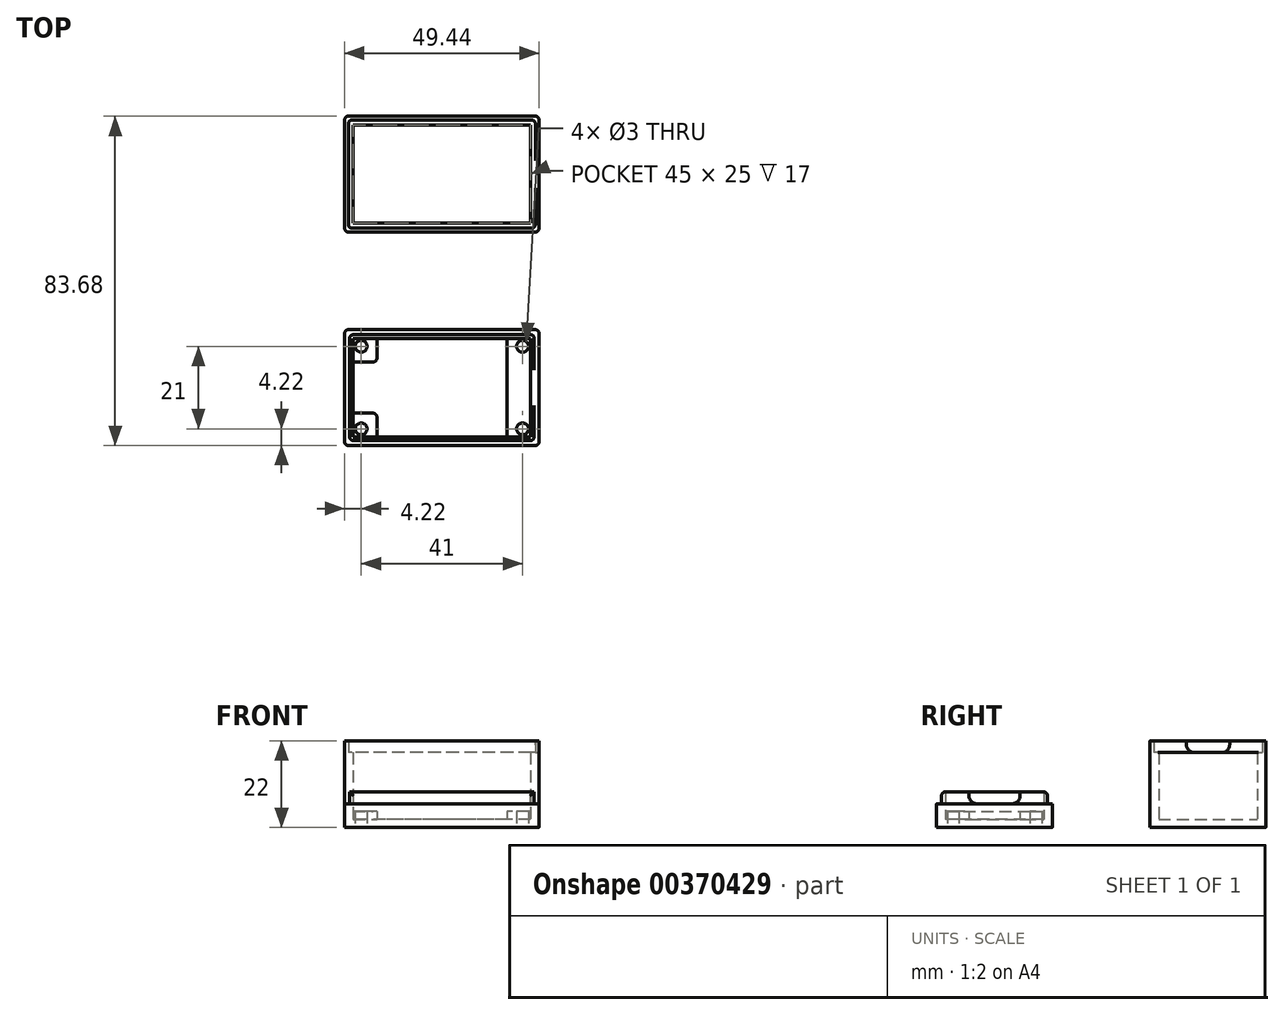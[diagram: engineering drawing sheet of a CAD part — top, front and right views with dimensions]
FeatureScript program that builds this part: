
annotation { "Feature Type Name" : "Feature", "Feature Type Description" : "" }
export const myFeature = defineFeature(function(context is Context, id is Id, definition is map)
    precondition{}
    {
        {
            var Q0;
            Q0=qCreatedBy(makeId("Top.planeOp"),FACE);
            var sketch = newSketch(context, id + "F0", { "sketchPlane" : qUnion([Q0])});
            skLineSegment(sketch, "E0.bottom", {"start": v(22.5, -12.5) * mm, "end": v(-22.5, -12.5) * mm});
            skLineSegment(sketch, "E0.top", {"start": v(22.5, 12.5) * mm, "end": v(-22.5, 12.5) * mm});
            skLineSegment(sketch, "E0.left", {"start": v(22.5, -12.5) * mm, "end": v(22.5, 12.5) * mm});
            skLineSegment(sketch, "E0.right", {"start": v(-22.5, -12.5) * mm, "end": v(-22.5, 12.5) * mm});
            skPoint(sketch, "E0.middle", {"position": v(0, 0) * mm});
            skPoint(sketch, "E1", {"position": v(20.5, 10.5) * mm});
            skPoint(sketch, "E2", {"position": v(-20.5, -10.5) * mm});
            skLineSegment(sketch, "E3", {"start": v(16.5, 12.5) * mm, "end": v(16.5, -12.5) * mm});
            skLineSegment(sketch, "E4", {"start": v(-22.5, 6.5) * mm, "end": v(-16.5, 6.5) * mm});
            skLineSegment(sketch, "E5", {"start": v(-16.5, 6.5) * mm, "end": v(-16.5, 12.5) * mm});
            skLineSegment(sketch, "E6", {"start": v(-22.5, -6.5) * mm, "end": v(-16.5, -6.5) * mm});
            skLineSegment(sketch, "E7", {"start": v(-16.5, -6.5) * mm, "end": v(-16.5, -12.5) * mm});
            skLineSegment(sketch, "E8.0", {"start": v(24.72, 14.72) * mm, "end": v(-24.72, 14.72) * mm});
            skLineSegment(sketch, "E8.1", {"start": v(24.72, -14.72) * mm, "end": v(24.72, 14.72) * mm});
            skLineSegment(sketch, "E8.2", {"start": v(24.72, -14.72) * mm, "end": v(-24.72, -14.72) * mm});
            skLineSegment(sketch, "E8.3", {"start": v(-24.72, -14.72) * mm, "end": v(-24.72, 14.72) * mm});
            skPoint(sketch, "E9", {"position": v(-20.5, 10.5) * mm});
            skPoint(sketch, "E10", {"position": v(20.5, -10.5) * mm});
            skLineSegment(sketch, "E11.bottom", {"start": v(22.5, 41.74) * mm, "end": v(-22.5, 41.74) * mm});
            skLineSegment(sketch, "E11.top", {"start": v(22.5, 66.74) * mm, "end": v(-22.5, 66.74) * mm});
            skLineSegment(sketch, "E11.left", {"start": v(22.5, 41.74) * mm, "end": v(22.5, 66.74) * mm});
            skLineSegment(sketch, "E11.right", {"start": v(-22.5, 41.74) * mm, "end": v(-22.5, 66.74) * mm});
            skPoint(sketch, "E11.middle", {"position": v(0, 54.24) * mm});
            skPoint(sketch, "E11.middle.positionSnap0", {"position": v(0, 12.5) * mm});
            skPoint(sketch, "E11.centerSnap0", {"position": v(0, 12.5) * mm});
            skLineSegment(sketch, "E12.0", {"start": v(24.72, 68.96) * mm, "end": v(-24.72, 68.96) * mm});
            skLineSegment(sketch, "E12.1", {"start": v(24.72, 39.52) * mm, "end": v(24.72, 68.96) * mm});
            skLineSegment(sketch, "E12.2", {"start": v(24.72, 39.52) * mm, "end": v(-24.72, 39.52) * mm});
            skLineSegment(sketch, "E12.3", {"start": v(-24.72, 39.52) * mm, "end": v(-24.72, 68.96) * mm});
            skSolve(sketch);
        }
        {
            var Q0;
            {var subQ0=sQuery(id+"F0.wireOp",EDGE,"E3");Q0=makeQuery(id+"F0.imprint","IMPRINT",FACE,{"disambiguationData":[TD([[makeQuery(id+"F0.imprint","IMPRINT",EDGE,{"derivedFrom":subQ0}),-1.0]])]});}
            extrude(context, id + "F1", {"entities" : qUnion([Q0]), "depth" : 2 * mm});
        }
        {
            var Q0;
            {var subQ4=sQuery(id+"F0.wireOp",EDGE,"E4");Q0=makeQuery(id+"F0.imprint","IMPRINT",FACE,{"disambiguationData":[TD([[makeQuery(id+"F0.imprint","IMPRINT",EDGE,{"derivedFrom":subQ4}),1.0]])]});}
            var Q1;
            {var subQ4=sQuery(id+"F0.wireOp",EDGE,"E6");Q1=makeQuery(id+"F0.imprint","IMPRINT",FACE,{"disambiguationData":[TD([[makeQuery(id+"F0.imprint","IMPRINT",EDGE,{"derivedFrom":subQ4}),-1.0]])]});}
            var Q2;
            {var subQ0=sQuery(id+"F0.wireOp",EDGE,"E0.left");Q2=makeQuery(id+"F0.imprint","IMPRINT",FACE,{"disambiguationData":[TD([[makeQuery(id+"F0.imprint","IMPRINT",EDGE,{"derivedFrom":subQ0}),1.0]])]});}
            extrude(context, id + "F2", {"entities" : qUnion([Q0, Q1, Q2]), "operationType" : NewBodyOperationType.ADD, "depth" : 4 * mm});
        }
        {
            var Q0;
            {var subQ7=sQuery(id+"F0.wireOp",EDGE,"E0.left");Q0=makeQuery(id+"F0.imprint","IMPRINT",FACE,{"disambiguationData":[TD([[makeQuery(id+"F0.imprint","IMPRINT",EDGE,{"derivedFrom":subQ7}),-1.0]])]});}
            extrude(context, id + "F3", {"entities" : qUnion([Q0]), "operationType" : NewBodyOperationType.ADD, "depth" : 6 * mm});
        }
        {
            var Q0;
            Q0=sQuery(id+"F0.wireOp",VERTEX,"E2");
            var Q1;
            Q1=sQuery(id+"F0.wireOp",VERTEX,"E1");
            var Q2;
            Q2=sQuery(id+"F0.wireOp",VERTEX,"E10");
            var Q3;
            Q3=sQuery(id+"F0.wireOp",VERTEX,"E9");
            var Q4;
            Q4=makeQuery(id+"F1.opExtrude","SWEPT_BODY",BODY,{"disambiguationData":[OSD([sQuery(id+"F0.wireOp",EDGE,"E0.bottom"),sQuery(id+"F0.wireOp",EDGE,"E0.top"),sQuery(id+"F0.wireOp",EDGE,"E0.right"),sQuery(id+"F0.wireOp",EDGE,"E3"),sQuery(id+"F0.wireOp",EDGE,"E4"),sQuery(id+"F0.wireOp",EDGE,"E5"),sQuery(id+"F0.wireOp",EDGE,"E6"),sQuery(id+"F0.wireOp",EDGE,"E7")])]});
            hole(context, id + "F4", {"style" : HoleStyle.SIMPLE, "endStyle" : HoleEndStyle.THROUGH, "oppositeDirection" : true, "holeDiameter" : 3 * mm, "isTappedThrough" : true, "tappedDepth" : 12 * mm, "tapClearance" : 3, "locations" : qUnion([Q0, Q1, Q2, Q3]), "scope" : qUnion([Q4])});
        }
        {
            var Q0;
            Q0=makeQuery(id+"F3.opExtrude","CAP_FACE",FACE,{"disambiguationData":[OSD([sQuery(id+"F0.wireOp",EDGE,"E0.bottom"),sQuery(id+"F0.wireOp",EDGE,"E0.top"),sQuery(id+"F0.wireOp",EDGE,"E0.left"),sQuery(id+"F0.wireOp",EDGE,"E0.right"),sQuery(id+"F0.wireOp",EDGE,"E8.0"),sQuery(id+"F0.wireOp",EDGE,"E8.1"),sQuery(id+"F0.wireOp",EDGE,"E8.2"),sQuery(id+"F0.wireOp",EDGE,"E8.3")])],"isStart":false});
            var sketch = newSketch(context, id + "F5", { "sketchPlane" : qUnion([Q0])});
            skLineSegment(sketch, "E13.0", {"start": v(23.46, 13.46) * mm, "end": v(-23.46, 13.46) * mm});
            skLineSegment(sketch, "E13.1", {"start": v(23.46, -13.46) * mm, "end": v(23.46, 13.46) * mm});
            skLineSegment(sketch, "E13.2", {"start": v(23.46, -13.46) * mm, "end": v(-23.46, -13.46) * mm});
            skLineSegment(sketch, "E13.3", {"start": v(-23.46, -13.46) * mm, "end": v(-23.46, 13.46) * mm});
            skSolve(sketch);
        }
        {
            var Q0;
            Q0=makeQuery(id+"F5.imprint","IMPRINT",FACE,{"disambiguationData":[TD([[makeQuery(id+"F5.imprint","IMPRINT",EDGE,{"derivedFrom":sQuery(id+"F5.wireOp",EDGE,"E13.0")}),1.0]])]});
            extrude(context, id + "F6", {"entities" : qUnion([Q0]), "operationType" : NewBodyOperationType.ADD, "depth" : 3 * mm});
        }
        {
            var Q0;
            Q0=makeQuery(id+"F13.opFillet","SPLIT",FACE,{"disambiguationData":[OD(0.0)],"derivedFrom":makeQuery(id+"F6.opExtrude","CAP_FACE",FACE,{"disambiguationData":[OSD([sQuery(id+"F0.wireOp",EDGE,"E0.bottom"),sQuery(id+"F0.wireOp",EDGE,"E0.top"),sQuery(id+"F0.wireOp",EDGE,"E0.left"),sQuery(id+"F0.wireOp",EDGE,"E0.right"),sQuery(id+"F5.wireOp",EDGE,"E13.0"),sQuery(id+"F5.wireOp",EDGE,"E13.1"),sQuery(id+"F5.wireOp",EDGE,"E13.2"),sQuery(id+"F5.wireOp",EDGE,"E13.3")])],"isStart":false})});
            var sketch = newSketch(context, id + "F7", { "sketchPlane" : qUnion([Q0])});
            skLineSegment(sketch, "E14", {"start": v(22.5, 6.5) * mm, "end": v(23.46, 6.5) * mm});
            skLineSegment(sketch, "E15", {"start": v(22.5, -6.5) * mm, "end": v(23.46, -6.5) * mm});
            skSolve(sketch);
        }
        {
            var Q0;
            {var subQ0=sQuery(id+"F7.wireOp",EDGE,"E14");Q0=makeQuery(id+"F7.imprint","IMPRINT",FACE,{"disambiguationData":[TD([[makeQuery(id+"F7.imprint","IMPRINT",EDGE,{"derivedFrom":subQ0}),-1.0]])]});}
            extrude(context, id + "F8", {"entities" : qUnion([Q0]), "operationType" : NewBodyOperationType.REMOVE, "oppositeDirection" : true, "depth" : 3 * mm});
        }
        {
            var Q0;
            Q0=makeQuery(id+"F0.imprint","IMPRINT",FACE,{"disambiguationData":[TD([[makeQuery(id+"F0.imprint","IMPRINT",EDGE,{"derivedFrom":sQuery(id+"F0.wireOp",EDGE,"E11.bottom")}),-1.0]])]});
            extrude(context, id + "F9", {"entities" : qUnion([Q0]), "depth" : 2 * mm});
        }
        {
            var Q0;
            Q0=makeQuery(id+"F0.imprint","IMPRINT",FACE,{"disambiguationData":[TD([[makeQuery(id+"F0.imprint","IMPRINT",EDGE,{"derivedFrom":sQuery(id+"F0.wireOp",EDGE,"E11.bottom")}),1.0]])]});
            extrude(context, id + "F10", {"entities" : qUnion([Q0]), "operationType" : NewBodyOperationType.ADD, "depth" : 19 * mm});
        }
        {
            var Q0;
            Q0=makeQuery(id+"F10.opExtrude","CAP_FACE",FACE,{"disambiguationData":[OSD([sQuery(id+"F0.wireOp",EDGE,"E11.bottom"),sQuery(id+"F0.wireOp",EDGE,"E11.top"),sQuery(id+"F0.wireOp",EDGE,"E11.left"),sQuery(id+"F0.wireOp",EDGE,"E11.right"),sQuery(id+"F0.wireOp",EDGE,"E12.0"),sQuery(id+"F0.wireOp",EDGE,"E12.1"),sQuery(id+"F0.wireOp",EDGE,"E12.2"),sQuery(id+"F0.wireOp",EDGE,"E12.3")])],"isStart":false});
            var sketch = newSketch(context, id + "F11", { "sketchPlane" : qUnion([Q0])});
            skLineSegment(sketch, "E16.0", {"start": v(23.76, 68) * mm, "end": v(-23.76, 68) * mm});
            skLineSegment(sketch, "E16.1", {"start": v(23.76, 40.48) * mm, "end": v(23.76, 68) * mm});
            skLineSegment(sketch, "E16.2", {"start": v(23.76, 40.48) * mm, "end": v(-23.76, 40.48) * mm});
            skLineSegment(sketch, "E16.3", {"start": v(-23.76, 40.48) * mm, "end": v(-23.76, 68) * mm});
            skSolve(sketch);
        }
        {
            var Q0;
            Q0=makeQuery(id+"F11.imprint","IMPRINT",FACE,{"disambiguationData":[TD([[makeQuery(id+"F11.imprint","IMPRINT",EDGE,{"derivedFrom":sQuery(id+"F11.wireOp",EDGE,"E16.0")}),-1.0]])]});
            extrude(context, id + "F12", {"entities" : qUnion([Q0]), "operationType" : NewBodyOperationType.ADD, "depth" : 3 * mm});
        }
        {
            var Q0;
            Q0=makeQuery(id+"F2.opExtrude","SWEPT_EDGE",EDGE,{"disambiguationData":[OSD([sQuery(id+"F0.wireOp",EDGE,"E4"),sQuery(id+"F0.wireOp",EDGE,"E5")])]});
            var Q1;
            Q1=makeQuery(id+"F2.opExtrude","SWEPT_EDGE",EDGE,{"disambiguationData":[OSD([sQuery(id+"F0.wireOp",EDGE,"E6"),sQuery(id+"F0.wireOp",EDGE,"E7")])]});
            var Q2;
            Q2=makeQuery(id+"F6.opExtrude","SWEPT_EDGE",EDGE,{"disambiguationData":[OSD([sQuery(id+"F5.wireOp",EDGE,"E13.0"),sQuery(id+"F5.wireOp",EDGE,"E13.3")])]});
            var Q3;
            Q3=makeQuery(id+"F6.opExtrude","SWEPT_EDGE",EDGE,{"disambiguationData":[OSD([sQuery(id+"F5.wireOp",EDGE,"E13.0"),sQuery(id+"F5.wireOp",EDGE,"E13.1")])]});
            var Q4;
            Q4=makeQuery(id+"F6.opExtrude","SWEPT_EDGE",EDGE,{"disambiguationData":[OSD([sQuery(id+"F5.wireOp",EDGE,"E13.2"),sQuery(id+"F5.wireOp",EDGE,"E13.3")])]});
            var Q5;
            Q5=makeQuery(id+"F6.opExtrude","SWEPT_EDGE",EDGE,{"disambiguationData":[OSD([sQuery(id+"F5.wireOp",EDGE,"E13.1"),sQuery(id+"F5.wireOp",EDGE,"E13.2")])]});
            var Q6;
            Q6=makeQuery(id+"F6.opExtrude","CAP_EDGE",EDGE,{"disambiguationData":[OSD([sQuery(id+"F5.wireOp",EDGE,"E13.2")])],"isStart":false});
            var Q7;
            Q7=makeQuery(id+"F6.opExtrude","CAP_EDGE",EDGE,{"disambiguationData":[OSD([sQuery(id+"F5.wireOp",EDGE,"E13.0")])],"isStart":false});
            var Q8;
            Q8=makeQuery(id+"F3.opExtrude","SWEPT_EDGE",EDGE,{"disambiguationData":[OSD([sQuery(id+"F0.wireOp",EDGE,"E8.2"),sQuery(id+"F0.wireOp",EDGE,"E8.3")])]});
            var Q9;
            Q9=makeQuery(id+"F3.opExtrude","SWEPT_EDGE",EDGE,{"disambiguationData":[OSD([sQuery(id+"F0.wireOp",EDGE,"E8.0"),sQuery(id+"F0.wireOp",EDGE,"E8.3")])]});
            var Q10;
            Q10=makeQuery(id+"F3.opExtrude","SWEPT_EDGE",EDGE,{"disambiguationData":[OSD([sQuery(id+"F0.wireOp",EDGE,"E8.1"),sQuery(id+"F0.wireOp",EDGE,"E8.2")])]});
            var Q11;
            Q11=makeQuery(id+"F3.opExtrude","SWEPT_EDGE",EDGE,{"disambiguationData":[OSD([sQuery(id+"F0.wireOp",EDGE,"E8.0"),sQuery(id+"F0.wireOp",EDGE,"E8.1")])]});
            var Q12;
            Q12=makeQuery(id+"F10.opExtrude","SWEPT_EDGE",EDGE,{"disambiguationData":[OSD([sQuery(id+"F0.wireOp",EDGE,"E12.2"),sQuery(id+"F0.wireOp",EDGE,"E12.3")])]});
            var Q13;
            Q13=makeQuery(id+"F10.opExtrude","SWEPT_EDGE",EDGE,{"disambiguationData":[OSD([sQuery(id+"F0.wireOp",EDGE,"E12.0"),sQuery(id+"F0.wireOp",EDGE,"E12.3")])]});
            var Q14;
            Q14=makeQuery(id+"F10.opExtrude","SWEPT_EDGE",EDGE,{"disambiguationData":[OSD([sQuery(id+"F0.wireOp",EDGE,"E12.0"),sQuery(id+"F0.wireOp",EDGE,"E12.1")])]});
            var Q15;
            Q15=makeQuery(id+"F10.opExtrude","SWEPT_EDGE",EDGE,{"disambiguationData":[OSD([sQuery(id+"F0.wireOp",EDGE,"E12.1"),sQuery(id+"F0.wireOp",EDGE,"E12.2")])]});
            var Q16;
            Q16=makeQuery(id+"F12.opExtrude","SWEPT_EDGE",EDGE,{"disambiguationData":[OSD([sQuery(id+"F11.wireOp",EDGE,"E16.0"),sQuery(id+"F11.wireOp",EDGE,"E16.3")])]});
            var Q17;
            Q17=makeQuery(id+"F12.opExtrude","SWEPT_EDGE",EDGE,{"disambiguationData":[OSD([sQuery(id+"F11.wireOp",EDGE,"E16.0"),sQuery(id+"F11.wireOp",EDGE,"E16.1")])]});
            var Q18;
            Q18=makeQuery(id+"F12.opExtrude","SWEPT_EDGE",EDGE,{"disambiguationData":[OSD([sQuery(id+"F11.wireOp",EDGE,"E16.1"),sQuery(id+"F11.wireOp",EDGE,"E16.2")])]});
            var Q19;
            Q19=makeQuery(id+"F12.opExtrude","SWEPT_EDGE",EDGE,{"disambiguationData":[OSD([sQuery(id+"F11.wireOp",EDGE,"E16.2"),sQuery(id+"F11.wireOp",EDGE,"E16.3")])]});
            fillet(context, id + "F13", {"entities" : qUnion([Q0, Q1, Q2, Q3, Q4, Q5, Q6, Q7, Q8, Q9, Q10, Q11, Q12, Q13, Q14, Q15, Q16, Q17, Q18, Q19]), "radius" : 1 * mm, "tangentPropagation" : true, "allowEdgeOverflow" : false});
        }
        {
            var Q0;
            Q0=makeQuery(id+"F12.opExtrude","CAP_FACE",FACE,{"disambiguationData":[OSD([sQuery(id+"F0.wireOp",EDGE,"E12.0"),sQuery(id+"F0.wireOp",EDGE,"E12.1"),sQuery(id+"F0.wireOp",EDGE,"E12.2"),sQuery(id+"F0.wireOp",EDGE,"E12.3"),sQuery(id+"F11.wireOp",EDGE,"E16.0"),sQuery(id+"F11.wireOp",EDGE,"E16.1"),sQuery(id+"F11.wireOp",EDGE,"E16.2"),sQuery(id+"F11.wireOp",EDGE,"E16.3")])],"isStart":false});
            var sketch = newSketch(context, id + "F14", { "sketchPlane" : qUnion([Q0])});
            skLineSegment(sketch, "E17", {"start": v(23.76, 59.74) * mm, "end": v(24.72, 59.74) * mm});
            skLineSegment(sketch, "E18", {"start": v(23.76, 48.74) * mm, "end": v(24.72, 48.74) * mm});
            skSolve(sketch);
        }
        {
            var Q0;
            {var subQ0=sQuery(id+"F14.wireOp",EDGE,"E17");Q0=makeQuery(id+"F14.imprint","IMPRINT",FACE,{"disambiguationData":[TD([[makeQuery(id+"F14.imprint","IMPRINT",EDGE,{"derivedFrom":subQ0}),-1.0]])]});}
            extrude(context, id + "F15", {"entities" : qUnion([Q0]), "operationType" : NewBodyOperationType.REMOVE, "oppositeDirection" : true, "depth" : 3 * mm});
        }
        {
            var Q0;
            Q0=makeQuery(id+"F8.boolean.opBoolean","COPY",EDGE,{"derivedFrom":makeQuery(id+"F8.opExtrude","CAP_EDGE",EDGE,{"disambiguationData":[OSD([sQuery(id+"F7.wireOp",EDGE,"E14")])],"isStart":false})});
            var Q1;
            Q1=makeQuery(id+"F8.boolean.opBoolean","COPY",EDGE,{"derivedFrom":makeQuery(id+"F8.opExtrude","CAP_EDGE",EDGE,{"disambiguationData":[OSD([sQuery(id+"F7.wireOp",EDGE,"E15")])],"isStart":false})});
            var Q2;
            Q2=makeQuery(id+"F15.boolean.opBoolean","COPY",EDGE,{"derivedFrom":makeQuery(id+"F15.opExtrude","CAP_EDGE",EDGE,{"disambiguationData":[OSD([sQuery(id+"F14.wireOp",EDGE,"E17")])],"isStart":false})});
            var Q3;
            Q3=makeQuery(id+"F15.boolean.opBoolean","COPY",EDGE,{"derivedFrom":makeQuery(id+"F15.opExtrude","CAP_EDGE",EDGE,{"disambiguationData":[OSD([sQuery(id+"F14.wireOp",EDGE,"E18")])],"isStart":false})});
            fillet(context, id + "F16", {"entities" : qUnion([Q0, Q1, Q2, Q3]), "radius" : 2 * mm, "tangentPropagation" : true, "allowEdgeOverflow" : false});
        }
    });
